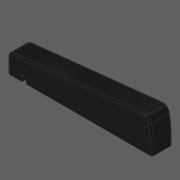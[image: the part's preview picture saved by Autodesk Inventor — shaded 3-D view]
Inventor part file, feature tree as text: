
AUTODESK INVENTOR PART (.ipt)
format: ipt  version: 2020 (Build 240168000, 168)  size: 253,440 bytes
history: native  units: in
note: dims shown in document units (in); Inventor stores cm internally (conversion verified against a paired STEP export)
features: other x3, extrude x3, fillet x2
ambient origin geometry x8: Origin, YZ Plane, XZ Plane, XY Plane, X Axis, Y Axis, Z Axis, Center Point
bodies: Solid1 (feature_tree)
feature tree (8):
  other  "Slot Start Plane"
  other  "Key Profile"
  extrude  "Key"  Depth=0.063in
  extrude  "Protrusion Cutout"  TaperAngle=0.0deg  [1 undecoded]
  fillet  "Front Fillet"  [1 undecoded]
  extrude  "Slot"  Depth=0.1181in
  fillet  "Edge Softening"  Radius=0.1374in
  other  "Slot Sketch"
note: 2 required parameter values undecoded (feature->parameter linkage not recoverable at this tier; creation-order binding heuristic only, values carry confidence <= 0.55)
